# Revit family: MFZ-KT50VG-E1(ET1)
name_source: partatom
category: Mechanical Equipment
revit_build: Autodesk Revit 2016 (Build: 20150714_1515(x64)
units: mm (PartAtom-declared; Revit-internal decimal feet)

## family parameters
Always vertical = Yes
Cut with Voids When Loaded = No
OmniClass Number = 23.75.00.00
OmniClass Title = Climate Control (HVAC)
Part Type = Normal
Room Calculation Point = No
Round Connector Dimension = Use Radius
Shared = No
Work Plane-Based = No

## types (1)
- MFZ-KT50VG-E1 (ET1)
    Air Direction = 4
    Cooling Air Flow 1_High (m3/h) = 624
    Cooling Air Flow 1_Low (m3/h) = 402
    Cooling Air Flow 1_Med. (m3/h) = 516
    Cooling Air Flow 1_Silent (m3/h) = 336
    Cooling Air Flow 1_Super High (m3/h) = 738
    Cooling Air Flow 2_High (m3/h) = 624
    Cooling Air Flow 2_Low (m3/h) = 402
    Cooling Air Flow 2_Med. (m3/h) = 516
    Cooling Air Flow 2_Silent (m3/h) = 336
    Cooling Air Flow 2_Super High (m3/h) = 738
    Cooling Fan Motor Current (A) = 0.32
    Cooling Fan Speed 1_High (rpm) = 970
    Cooling Fan Speed 1_Low (rpm) = 670
    Cooling Fan Speed 1_Med. (rpm) = 820
    Cooling Fan Speed 1_Silent (rpm) = 580
    Cooling Fan Speed 1_Super High (rpm) = 1120
    Cooling Fan Speed 2_High (rpm) = 970
    Cooling Fan Speed 2_Low (rpm) = 670
    Cooling Fan Speed 2_Med. (rpm) = 820
    Cooling Fan Speed 2_Silent (rpm) = 580
    Cooling Fan Speed 2_Super High (rpm) = 1120
    Cooling Power Input (W) = 37 W
    Cooling Running Current (A) = 0.34
    Cooling Sound Level 1_High (db(A)) = 42
    Cooling Sound Level 1_Low (db(A)) = 32
    Cooling Sound Level 1_Med. (db(A)) = 37
    Cooling Sound Level 1_Silent (db(A)) = 28
    Cooling Sound Level 1_Super High (db(A)) = 48
    Cooling Sound Level 2_High (db(A)) = 42
    Cooling Sound Level 2_Low (db(A)) = 32
    Cooling Sound Level 2_Med. (db(A)) = 37
    Cooling Sound Level 2_Silent (db(A)) = 28
    Cooling Sound Level 2_Super High (db(A)) = 48
    Depth (mm) = 215 mm
    Drain pipe_radius (mm) = 8 mm  [stored 0.0262467 ft]
    Fan Motor Model = RC0J40-P#
    Fan Speed Regulator = 5
    Gas pipe_radius (mm) = 6.35 mm  [stored 0.0208333 ft]
    Heating Air Flow 1_High (m3/h) = 696
    Heating Air Flow 1_Low (m3/h) = 462
    Heating Air Flow 1_Med. (m3/h) = 564
    Heating Air Flow 1_Silent (m3/h) = 360
    Heating Air Flow 1_Super High (m3/h) = 840
    Heating Air Flow 2_High (m3/h) = 696
    Heating Air Flow 2_Low (m3/h) = 462
    Heating Air Flow 2_Med. (m3/h) = 564
    Heating Air Flow 2_Silent (m3/h) = 360
    Heating Air Flow 2_Super High (m3/h) = 840
    Heating Fan Motor Current (A) = 0.43
    Heating Fan Speed 1_High (rpm) = 1060
    Heating Fan Speed 1_Low (rpm) = 750
    Heating Fan Speed 1_Med. (rpm) = 890
    Heating Fan Speed 1_Silent (rpm) = 610
    Heating Fan Speed 1_Super High (rpm) = 1250
    Heating Fan Speed 2_High (rpm) = 1060
    Heating Fan Speed 2_Low (rpm) = 750
    Heating Fan Speed 2_Med. (rpm) = 890
    Heating Fan Speed 2_Silent (rpm) = 610
    Heating Fan Speed 2_Super High (rpm) = 1250
    Heating Power Input (W) = 52 W
    Heating Running Current (A) = 0.45
    Heating Sound Level 1_Hgh (db(A)) = 44
    Heating Sound Level 1_Low (db(A)) = 35
    Heating Sound Level 1_Med. (db(A)) = 40
    Heating Sound Level 1_Silent (dB(A)) = 29
    Heating Sound Level 1_Super Hgh (db(A)) = 49
    Heating Sound Level 2_Hgh (db(A)) = 44
    Heating Sound Level 2_Low (db(A)) = 35
    Heating Sound Level 2_Med. (db(A)) = 40
    Heating Sound Level 2_Silent (dB(A)) = 29
    Heating Sound Level 2_Super Hgh (db(A)) = 49
    Height (mm) = 600 mm
    Hertz = 50 Hz
    Liquid pipe_radius (mm) = 3.175 mm  [stored 0.0104167 ft]
    Manufacturer = Mitsubishi Electric Corporation
    Model = MFZ-KT50VG
    Phase = 1
    Remote Controller Model = SG191
    Space View = Yes
    Subcategory = HVAC
    URL = http://www.mitsubishielectric.com
    Unit Weight (kg) = 14.5
    Voltage = 230 V
    Width (mm) = 750 mm  [stored 2.46063 ft]

note: [stored X ft] marks values corroborated as IEEE doubles in the binary element streams (Revit-internal decimal feet)

## geometry (parser evidence)
native form markers: Blend x40, Sweep x2
no freeform markers — native parametric forms only
